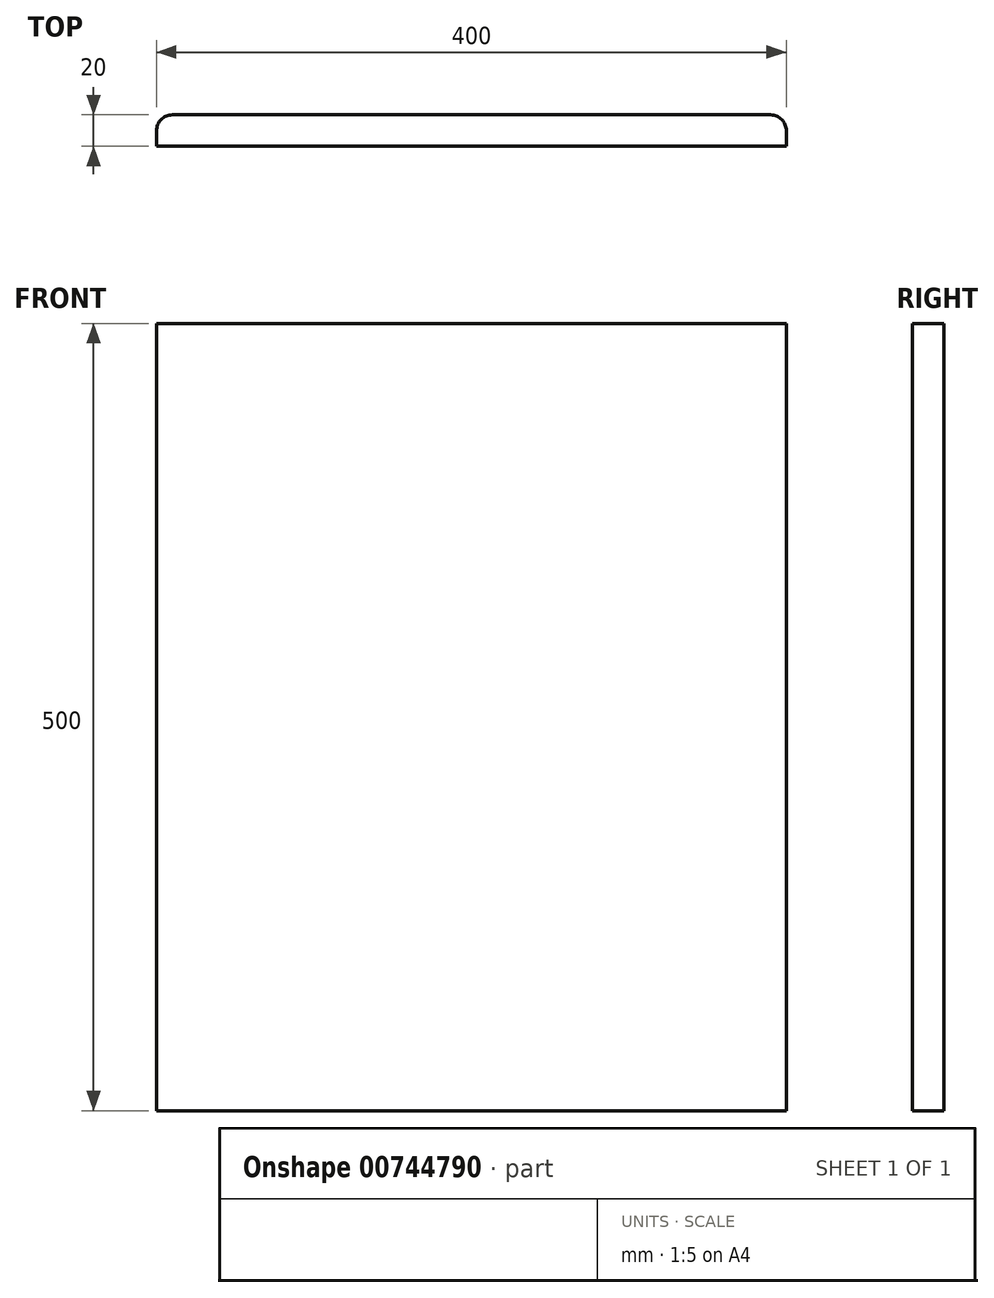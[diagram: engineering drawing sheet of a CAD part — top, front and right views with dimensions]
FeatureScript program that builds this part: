
annotation { "Feature Type Name" : "Feature", "Feature Type Description" : "" }
export const myFeature = defineFeature(function(context is Context, id is Id, definition is map)
    precondition{}
    {
        {
            var Q0;
            Q0=qCreatedBy(makeId("Top.planeOp"),FACE);
            var sketch = newSketch(context, id + "F0", { "sketchPlane" : qUnion([Q0])});
            skLineSegment(sketch, "E0.bottom", {"start": v(-190, 20) * mm, "end": v(190, 20) * mm});
            skLineSegment(sketch, "E0.top", {"start": v(-200, 0) * mm, "end": v(200, 0) * mm});
            skLineSegment(sketch, "E0.left", {"start": v(-200, 10) * mm, "end": v(-200, 0) * mm});
            skLineSegment(sketch, "E0.right", {"start": v(200, 10) * mm, "end": v(200, 0) * mm});
            skPoint(sketch, "E1.visualSharp", {"position": v(-200, 20) * mm});
            skArc(sketch, "E1.filletArc", {"start": v(-190, 20) * mm, "mid": v(-197.07, 17.07) * mm, "end": v(-200, 10) * mm});
            skPoint(sketch, "E2.visualSharp", {"position": v(200, 20) * mm});
            skArc(sketch, "E2.filletArc", {"start": v(200, 10) * mm, "mid": v(197.07, 17.07) * mm, "end": v(190, 20) * mm});
            skSolve(sketch);
        }
        {
            var Q0;
            Q0=makeQuery(id+"F0.imprint","IMPRINT",FACE,{"disambiguationData":[TD([[makeQuery(id+"F0.imprint","IMPRINT",EDGE,{"derivedFrom":sQuery(id+"F0.wireOp",EDGE,"E0.bottom")}),-1.0]])]});
            extrude(context, id + "F1", {"entities" : qUnion([Q0]), "depth" : 500 * mm, "offsetDistance" : 25 * mm});
        }
    });
